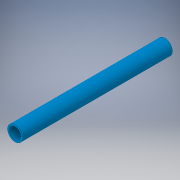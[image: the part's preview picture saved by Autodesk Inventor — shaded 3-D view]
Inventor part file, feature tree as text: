
AUTODESK INVENTOR PART (.ipt)
format: ipt  version: 2018 (Build 220112000, 112)  size: 106,496 bytes
history: native  units: in
note: dims shown in document units (in); Inventor stores cm internally (conversion verified against a paired STEP export)
features: extrude x1, sketch x1
ambient origin geometry x8: Origin, YZ Plane, XZ Plane, XY Plane, X Axis, Y Axis, Z Axis, Center Point
bodies: Solid1 (feature_tree)
feature tree (2):
  extrude  "Extrusion1"  Depth=13.0in
  sketch  "Sketch1"  dims[d0=1.315in d1=1.0in d2=13.0in d3=0.0in]
